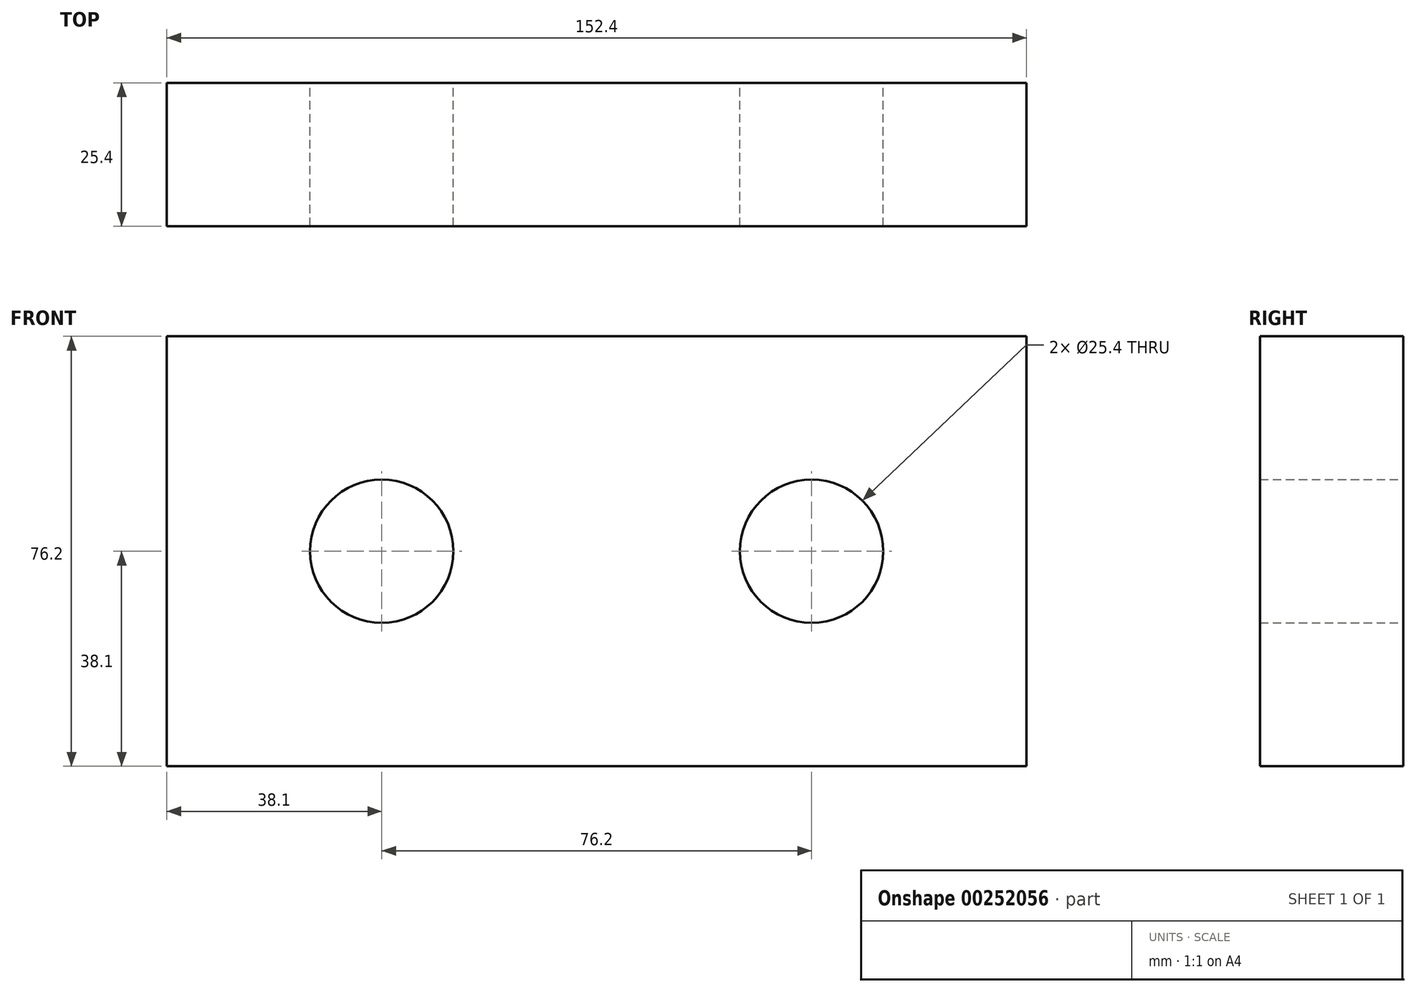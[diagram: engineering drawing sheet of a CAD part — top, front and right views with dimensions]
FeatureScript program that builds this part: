
annotation { "Feature Type Name" : "Feature", "Feature Type Description" : "" }
export const myFeature = defineFeature(function(context is Context, id is Id, definition is map)
    precondition{}
    {
        {
            var Q0;
            Q0=qCreatedBy(makeId("Front.planeOp"),FACE);
            var sketch = newSketch(context, id + "F0", { "sketchPlane" : qUnion([Q0])});
            skLineSegment(sketch, "E0.bottom", {"start": v(76.2, -38.1) * mm, "end": v(-76.2, -38.1) * mm});
            skLineSegment(sketch, "E0.top", {"start": v(76.2, 38.1) * mm, "end": v(-76.2, 38.1) * mm});
            skLineSegment(sketch, "E0.left", {"start": v(76.2, -38.1) * mm, "end": v(76.2, 38.1) * mm});
            skLineSegment(sketch, "E0.right", {"start": v(-76.2, -38.1) * mm, "end": v(-76.2, 38.1) * mm});
            skPoint(sketch, "E0.middle", {"position": v(0, 0) * mm});
            skLineSegment(sketch, "E1", {"start": v(0, 0) * mm, "end": v(-38.1, 0) * mm});
            skCircle(sketch, "E2", {"center": v(-38.1, 0) * mm, "radius": 12.7 * mm});
            skLineSegment(sketch, "E3", {"start": v(0, 0) * mm, "end": v(38.1, 0) * mm});
            skCircle(sketch, "E4", {"center": v(38.1, 0) * mm, "radius": 12.7 * mm});
            skSolve(sketch);
        }
        {
            var Q0;
            Q0 = qSketchRegion(id + "F0", true);
            extrude(context, id + "F1", {"entities" : qUnion([Q0]), "depth" : 25.4 * mm});
        }
    });
